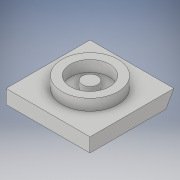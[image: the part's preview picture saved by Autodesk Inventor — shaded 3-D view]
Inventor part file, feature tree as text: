
AUTODESK INVENTOR PART (.ipt)
format: ipt  version: 2018 (Build 220112000, 112)  size: 126,464 bytes
history: native  units: in
note: dims shown in document units (in); Inventor stores cm internally (conversion verified against a paired STEP export)
features: extrude x4, sketch x4
ambient origin geometry x8: Origin, YZ Plane, XZ Plane, XY Plane, X Axis, Y Axis, Z Axis, Center Point
bodies: Solid1 (feature_tree)
feature tree (8):
  extrude  "Extrusion1"  Depth=1.1811in
  extrude  "Extrusion2"  Depth=0.1969in
  extrude  "Extrusion3"  Depth=0.0984in
  extrude  "Extrusion4"  Depth=0.1575in TaperAngle=0.0deg
  sketch  "Sketch1"  dims[d0=1.1811in d1=1.1811in]
  sketch  "Sketch2"  dims[d2=0.1969in d3=0.0in d4=0.2165in]
  sketch  "Sketch3"  dims[d5=0.0984in d6=0.0in d7=0.5512in]
  sketch  "Sketch4"  dims[d8=0.7874in d9=0.1575in d10=0.0in d12=120.0deg d13=1.1811in d14=0.0in]
